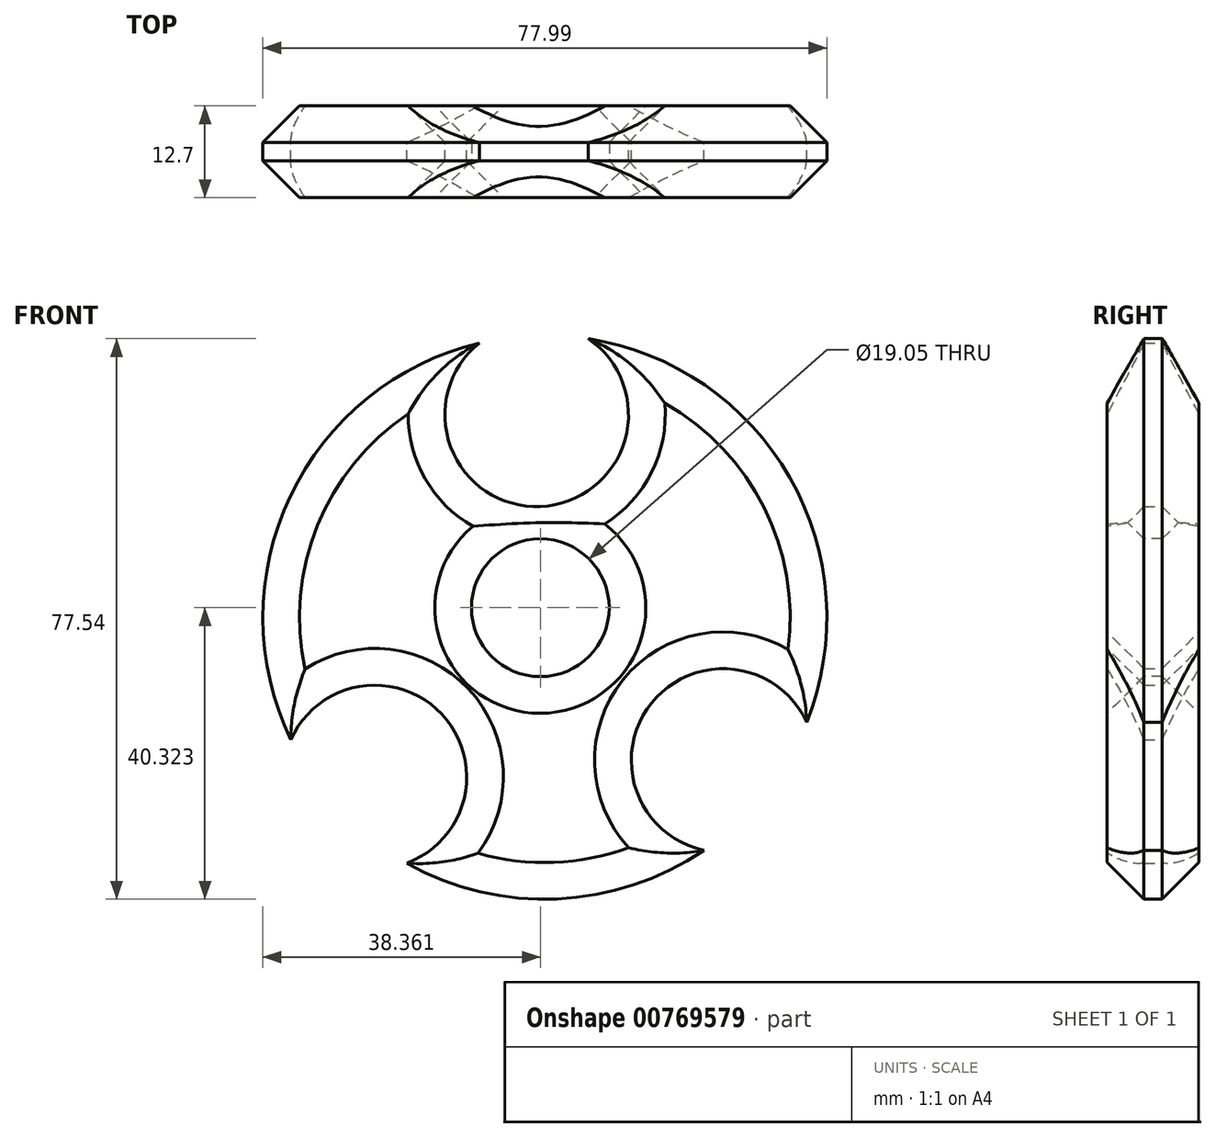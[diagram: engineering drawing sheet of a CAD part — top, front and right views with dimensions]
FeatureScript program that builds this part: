
annotation { "Feature Type Name" : "Feature", "Feature Type Description" : "" }
export const myFeature = defineFeature(function(context is Context, id is Id, definition is map)
    precondition{}
    {
        {
            var Q0;
            Q0=qCreatedBy(makeId("Front.planeOp"),FACE);
            var sketch = newSketch(context, id + "F0", { "sketchPlane" : qUnion([Q0])});
            skCircle(sketch, "E0", {"center": v(-14.65, 18.2) * mm, "radius": 39 * mm});
            skSolve(sketch);
        }
        {
            var Q0;
            Q0=makeQuery(id+"F0.imprint","IMPRINT",FACE,{"disambiguationData":[TD([[makeQuery(id+"F0.imprint","IMPRINT",EDGE,{"derivedFrom":sQuery(id+"F0.wireOp",EDGE,"E0")}),1.0]])]});
            var sketch = newSketch(context, id + "F1", { "sketchPlane" : qUnion([Q0])});
            skPoint(sketch, "E1", {"position": v(-15.79, 46.2) * mm});
            skPoint(sketch, "E2", {"position": v(10, -1.61) * mm});
            skPoint(sketch, "E3", {"position": v(-38.17, -3.9) * mm});
            skSolve(sketch);
        }
        {
            var Q0;
            Q0=makeQuery(id+"F0.imprint","IMPRINT",FACE,{"disambiguationData":[TD([[makeQuery(id+"F0.imprint","IMPRINT",EDGE,{"derivedFrom":sQuery(id+"F0.wireOp",EDGE,"E0")}),1.0]])]});
            extrude(context, id + "F2", {"entities" : qUnion([Q0]), "depth" : 12.7 * mm, "offsetDistance" : 25.4 * mm});
        }
        {
            var Q0;
            Q0=sQuery(id+"F1.wireOp",VERTEX,"E1");
            var Q1;
            Q1=sQuery(id+"F1.wireOp",VERTEX,"E3");
            var Q2;
            Q2=sQuery(id+"F1.wireOp",VERTEX,"E2");
            var Q3;
            Q3=makeQuery(id+"F2.opExtrude","SWEPT_BODY",BODY,{"disambiguationData":[OSD([sQuery(id+"F0.wireOp",EDGE,"E0")])]});
            hole(context, id + "F3", {"style" : HoleStyle.SIMPLE, "endStyle" : HoleEndStyle.THROUGH, "oppositeDirection" : true, "holeDiameter" : 25.4 * mm, "majorDiameter" : 6.35 * mm, "isTappedThrough" : true, "tappedDepth" : 12.7 * mm, "tapClearance" : 3, "locations" : qUnion([Q0, Q1, Q2]), "scope" : qUnion([Q3])});
        }
        {
            var Q0;
            Q0=makeQuery(id+"F2.opExtrude","CAP_FACE",FACE,{"disambiguationData":[OSD([sQuery(id+"F0.wireOp",EDGE,"E0")])],"isStart":false});
            var sketch = newSketch(context, id + "F4", { "sketchPlane" : qUnion([Q0])});
            skPoint(sketch, "E4", {"position": v(-15.29, 19.51) * mm});
            skSolve(sketch);
        }
        {
            var Q0;
            Q0=sQuery(id+"F4.wireOp",VERTEX,"E4");
            var Q1;
            Q1=makeQuery(id+"F2.opExtrude","SWEPT_BODY",BODY,{"disambiguationData":[OSD([sQuery(id+"F0.wireOp",EDGE,"E0")])]});
            hole(context, id + "F5", {"style" : HoleStyle.SIMPLE, "endStyle" : HoleEndStyle.THROUGH, "holeDiameter" : 19.05 * mm, "majorDiameter" : 6.35 * mm, "isTappedThrough" : true, "tappedDepth" : 12.7 * mm, "tapClearance" : 3, "locations" : qUnion([Q0]), "scope" : qUnion([Q1])});
        }
        {
            var Q0;
            Q0=makeQuery(id+"F2.opExtrude","CAP_FACE",FACE,{"disambiguationData":[OSD([sQuery(id+"F0.wireOp",EDGE,"E0")])],"isStart":false});
            chamfer(context, id + "F6", {"entities" : qUnion([Q0]), "width" : 5.08 * mm, "tangentPropagation" : true});
        }
        {
            var Q0;
            Q0=makeQuery(id+"F2.opExtrude","CAP_FACE",FACE,{"disambiguationData":[OSD([sQuery(id+"F0.wireOp",EDGE,"E0")])],"isStart":true});
            chamfer(context, id + "F7", {"entities" : qUnion([Q0]), "width" : 5.08 * mm, "tangentPropagation" : true});
        }
    });
